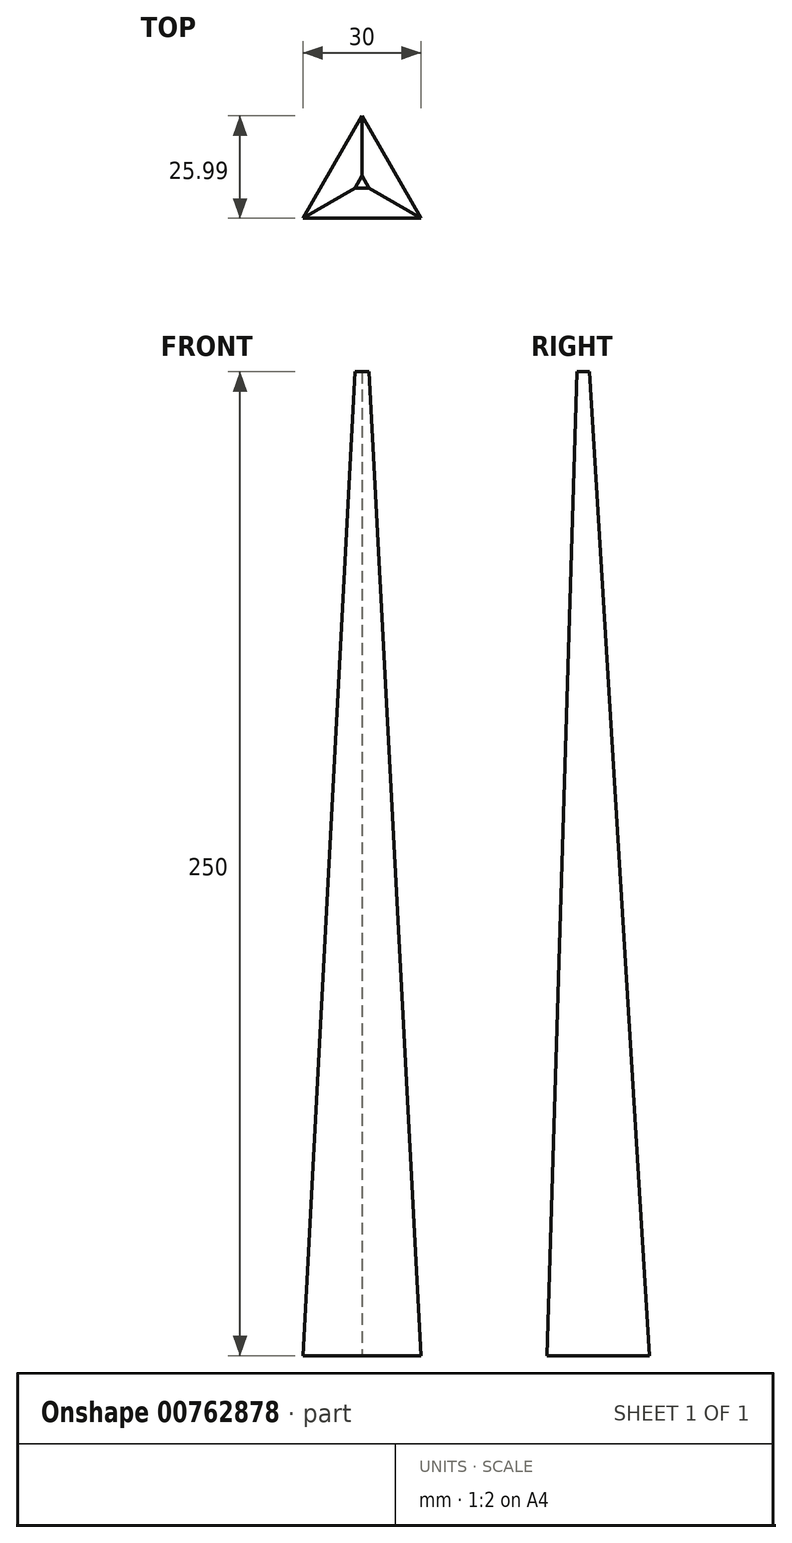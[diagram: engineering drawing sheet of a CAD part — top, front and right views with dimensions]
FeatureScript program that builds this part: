
annotation { "Feature Type Name" : "Feature", "Feature Type Description" : "" }
export const myFeature = defineFeature(function(context is Context, id is Id, definition is map)
    precondition{}
    {
        {
            var Q0;
            Q0=qCreatedBy(makeId("Top.planeOp"),FACE);
            var sketch = newSketch(context, id + "F0", { "sketchPlane" : qUnion([Q0])});
            skLineSegment(sketch, "E0", {"start": v(-43.88, 44.79) * mm, "end": v(-58.88, 18.8) * mm});
            skLineSegment(sketch, "E1", {"start": v(-58.88, 18.8) * mm, "end": v(-28.88, 18.8) * mm});
            skLineSegment(sketch, "E2", {"start": v(-28.88, 18.8) * mm, "end": v(-43.88, 44.79) * mm});
            skSolve(sketch);
        }
        {
            var Q0;
            Q0=makeQuery(id+"F0.imprint","IMPRINT",FACE,{"disambiguationData":[TD([[makeQuery(id+"F0.imprint","IMPRINT",EDGE,{"derivedFrom":sQuery(id+"F0.wireOp",EDGE,"E0")}),1.0]])]});
            extrude(context, id + "F1", {"entities" : qUnion([Q0]), "depth" : 250 * mm, "offsetDistance" : 25.4 * mm});
        }
        {
            var Q0;
            Q0=makeQuery(id+"F1.opExtrude","CAP_EDGE",EDGE,{"disambiguationData":[OSD([sQuery(id+"F0.wireOp",EDGE,"E0")])],"isStart":false});
            chamfer(context, id + "F2", {"entities" : qUnion([Q0]), "chamferType" : ChamferType.TWO_OFFSETS, "width1" : 7.62 * mm, "oppositeDirection" : false, "width2" : 250 * mm, "tangentPropagation" : true});
        }
        {
            var Q0;
            Q0=makeQuery(id+"F1.opExtrude","CAP_EDGE",EDGE,{"disambiguationData":[OSD([sQuery(id+"F0.wireOp",EDGE,"E2")])],"isStart":false});
            chamfer(context, id + "F3", {"entities" : qUnion([Q0]), "chamferType" : ChamferType.TWO_OFFSETS, "width1" : 7.62 * mm, "oppositeDirection" : false, "width2" : 250 * mm, "tangentPropagation" : true});
        }
        {
            var Q0;
            Q0=makeQuery(id+"F1.opExtrude","CAP_EDGE",EDGE,{"disambiguationData":[OSD([sQuery(id+"F0.wireOp",EDGE,"E1")])],"isStart":false});
            chamfer(context, id + "F4", {"entities" : qUnion([Q0]), "chamferType" : ChamferType.TWO_OFFSETS, "width1" : 7.62 * mm, "oppositeDirection" : false, "width2" : 250 * mm, "tangentPropagation" : true});
        }
    });
